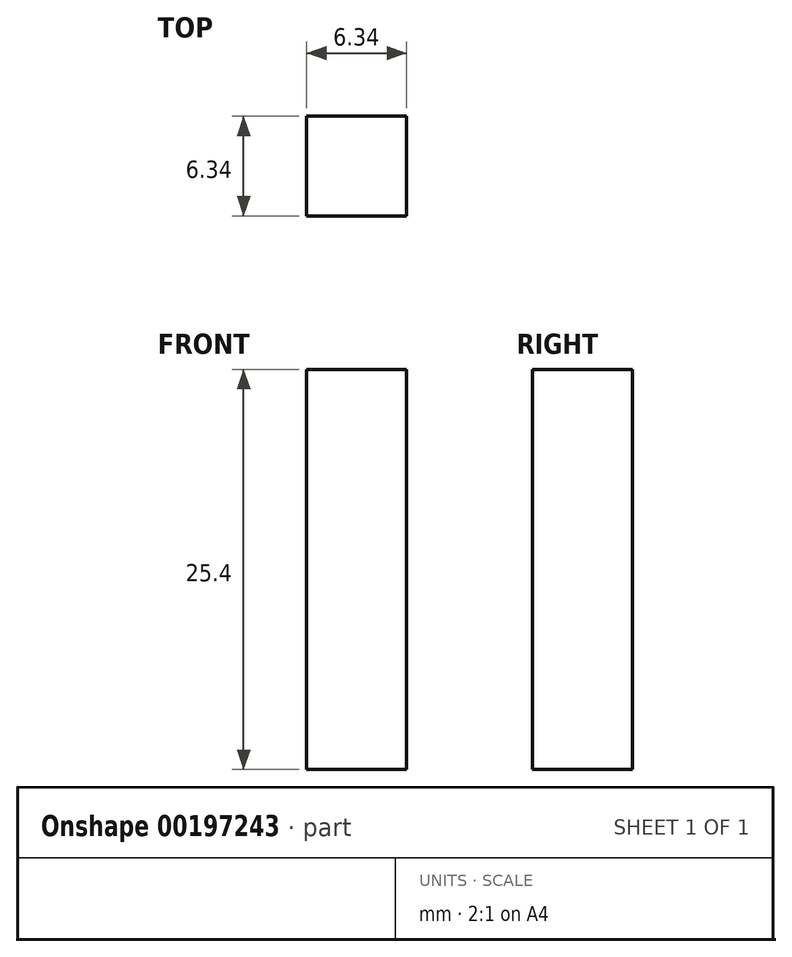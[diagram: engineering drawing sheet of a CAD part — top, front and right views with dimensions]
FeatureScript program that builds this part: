
annotation { "Feature Type Name" : "Feature", "Feature Type Description" : "" }
export const myFeature = defineFeature(function(context is Context, id is Id, definition is map)
    precondition{}
    {
        {
            var Q0;
            Q0=qCreatedBy(makeId("Top.planeOp"),FACE);
            var sketch = newSketch(context, id + "F0", { "sketchPlane" : qUnion([Q0])});
            skLineSegment(sketch, "E0.bottom", {"start": v(-3.17, 3.18) * mm, "end": v(3.18, 3.18) * mm});
            skLineSegment(sketch, "E0.top", {"start": v(-3.18, -3.17) * mm, "end": v(3.17, -3.17) * mm});
            skLineSegment(sketch, "E0.left", {"start": v(-3.17, 3.17) * mm, "end": v(-3.18, -3.17) * mm});
            skLineSegment(sketch, "E0.right", {"start": v(3.18, 3.18) * mm, "end": v(3.17, -3.17) * mm});
            skPoint(sketch, "E0.middle", {"position": v(0, 0) * mm});
            skSolve(sketch);
        }
        {
            var Q0;
            Q0=makeQuery(id+"F0.imprint","IMPRINT",FACE,{"disambiguationData":[TD([[makeQuery(id+"F0.imprint","IMPRINT",EDGE,{"derivedFrom":sQuery(id+"F0.wireOp",EDGE,"E0.bottom")}),-1.0]])]});
            extrude(context, id + "F1", {"entities" : qUnion([Q0]), "depth" : 25.4 * mm});
        }
    });
